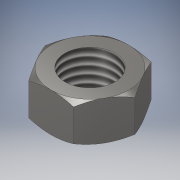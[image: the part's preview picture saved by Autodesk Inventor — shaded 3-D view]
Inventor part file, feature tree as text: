
AUTODESK INVENTOR PART (.ipt)
format: ipt  version: 2018 (Build 220112000, 112)  size: 151,040 bytes
history: native  units: in
note: dims shown in document units (in); Inventor stores cm internally (conversion verified against a paired STEP export)
features: sketch x2, extrude x1, revolve x1, hole x1, projected_geometry x1
ambient origin geometry x8: Origin, YZ Plane, XZ Plane, XY Plane, X Axis, Y Axis, Z Axis, Center Point
bodies: Solid1 (feature_tree)
feature tree (6):
  extrude  "Extrusion2"  Depth=1.0in
  revolve  "Revolution3"  Angle=90.0deg
  hole  "Hole1"  [1 undecoded]
  sketch  "Sketch3"  dims[d9=0.5in d10=0.0in d15=1.0in]
  sketch  "Sketch5"  dims[d16=30.0deg d17=90.0deg d28=1.0in d29=1.0in d20=0.642in d21=1.5in d22=0.375in d23=0.25in d24=0.5635in d25=2.0in d26=0.8108in d27=1.0in]
  projected_geometry  "Projected Loop2"
note: 1 required parameter value undecoded (feature->parameter linkage not recoverable at this tier; creation-order binding heuristic only, values carry confidence <= 0.55)
